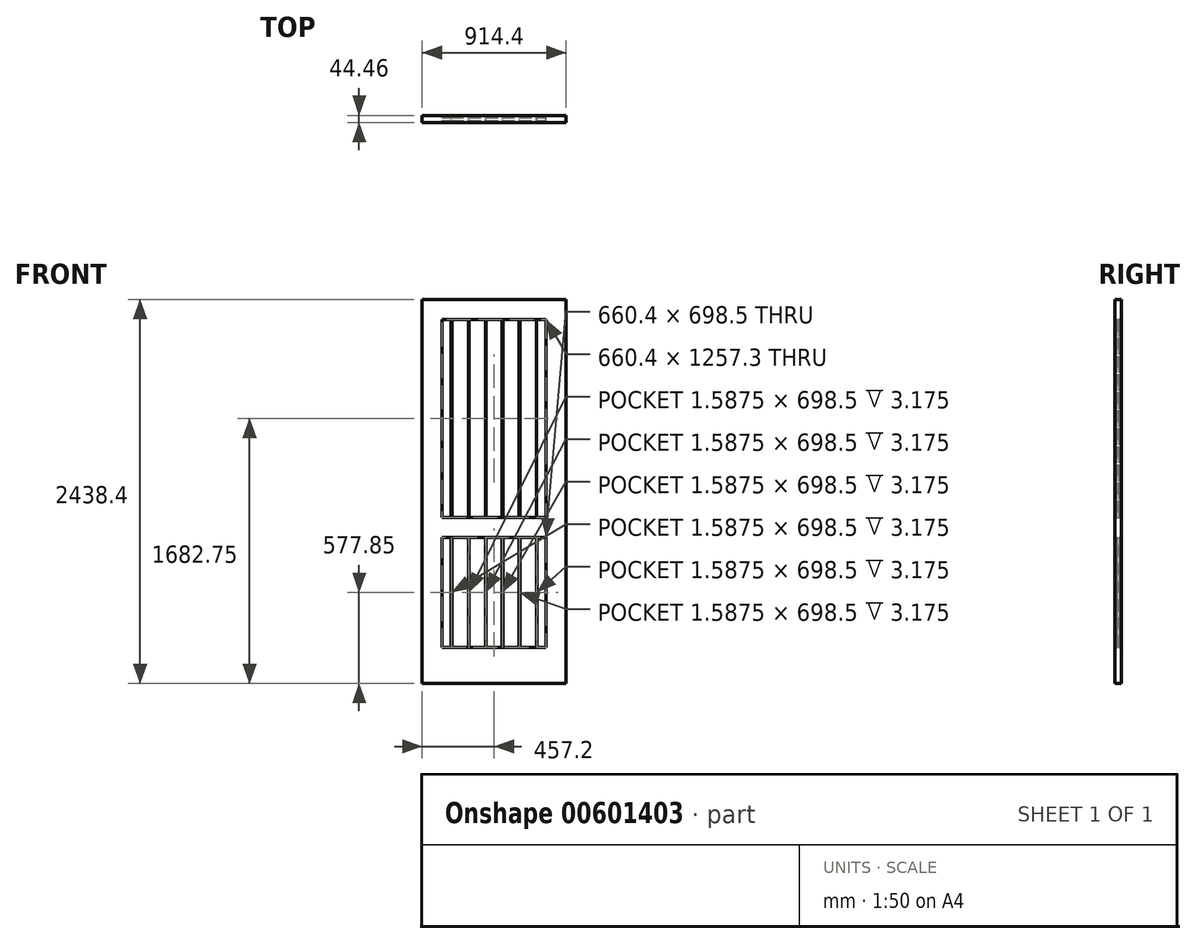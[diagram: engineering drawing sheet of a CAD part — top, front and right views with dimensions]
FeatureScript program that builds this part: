
annotation { "Feature Type Name" : "Feature", "Feature Type Description" : "" }
export const myFeature = defineFeature(function(context is Context, id is Id, definition is map)
    precondition{}
    {
        {
            var Q0;
            Q0=qCreatedBy(makeId("Front.planeOp"),FACE);
            var sketch = newSketch(context, id + "F0", { "sketchPlane" : qUnion([Q0])});
            skLineSegment(sketch, "E0.bottom", {"start": v(-457.2, 1219.2) * mm, "end": v(457.2, 1219.2) * mm});
            skLineSegment(sketch, "E0.top", {"start": v(-457.2, -1219.2) * mm, "end": v(457.2, -1219.2) * mm});
            skLineSegment(sketch, "E0.left", {"start": v(-457.2, 1219.2) * mm, "end": v(-457.2, -1219.2) * mm});
            skLineSegment(sketch, "E0.right", {"start": v(457.2, 1219.2) * mm, "end": v(457.2, -1219.2) * mm});
            skPoint(sketch, "E0.middle", {"position": v(0, 0) * mm});
            skLineSegment(sketch, "E1.bottom", {"start": v(-330.2, 1092.2) * mm, "end": v(330.2, 1092.2) * mm});
            skLineSegment(sketch, "E1.top", {"start": v(-330.2, -990.6) * mm, "end": v(330.2, -990.6) * mm});
            skLineSegment(sketch, "E1.left", {"start": v(-330.2, 1092.2) * mm, "end": v(-330.2, -990.6) * mm});
            skLineSegment(sketch, "E1.right", {"start": v(330.2, 1092.2) * mm, "end": v(330.2, -990.6) * mm});
            skPoint(sketch, "E1.middle", {"position": v(0, 50.8) * mm});
            skLineSegment(sketch, "E2", {"start": v(-330.2, -292.1) * mm, "end": v(330.2, -292.1) * mm});
            skLineSegment(sketch, "E3", {"start": v(-330.2, -165.1) * mm, "end": v(330.2, -165.1) * mm});
            skLineSegment(sketch, "E4", {"start": v(0, 1219.2) * mm, "end": v(0, -990.6) * mm, "construction": true});
            skLineSegment(sketch, "E5", {"start": v(-53.97, 1092.2) * mm, "end": v(-53.98, -165.1) * mm});
            skLineSegment(sketch, "E6", {"start": v(-161.92, 1092.2) * mm, "end": v(-161.92, -165.1) * mm});
            skLineSegment(sketch, "E7", {"start": v(-269.87, 1092.2) * mm, "end": v(-269.87, -165.1) * mm});
            skLineSegment(sketch, "E8.MirrorCS", {"start": v(53.98, 1092.2) * mm, "end": v(53.97, -165.1) * mm});
            skLineSegment(sketch, "E9.MirrorCS", {"start": v(161.92, 1092.2) * mm, "end": v(161.92, -165.1) * mm});
            skLineSegment(sketch, "E10.MirrorCS", {"start": v(269.87, 1092.2) * mm, "end": v(269.87, -165.1) * mm});
            skLineSegment(sketch, "E11", {"start": v(-330.2, -235.67) * mm, "end": v(330.2, -235.67) * mm, "construction": true});
            skLineSegment(sketch, "E12.trimOffspring", {"start": v(-269.88, -990.6) * mm, "end": v(-269.87, -292.1) * mm});
            skLineSegment(sketch, "E13.trimOffspring", {"start": v(-161.93, -990.6) * mm, "end": v(-161.92, -292.1) * mm});
            skLineSegment(sketch, "E14.trimOffspring", {"start": v(-53.97, -990.6) * mm, "end": v(-53.97, -292.1) * mm});
            skLineSegment(sketch, "E15.trimOffspring", {"start": v(53.97, -990.6) * mm, "end": v(53.98, -292.1) * mm});
            skLineSegment(sketch, "E16.trimOffspring", {"start": v(269.87, -990.6) * mm, "end": v(269.88, -292.1) * mm});
            skPoint(sketch, "E17.MirrorCS.start.orphan", {"position": v(-53.98, -1563.55) * mm});
            skPoint(sketch, "E18.MirrorCS.start.orphan", {"position": v(53.97, -1563.55) * mm});
            skPoint(sketch, "E19.MirrorCS.start.orphan", {"position": v(161.93, -1563.55) * mm});
            skPoint(sketch, "E20.MirrorCS.start.orphan", {"position": v(269.88, -1563.55) * mm});
            skPoint(sketch, "E21.MirrorCS.start.orphan", {"position": v(-161.93, -1563.55) * mm});
            skPoint(sketch, "E22.MirrorCS.start.orphan", {"position": v(-269.88, -1563.55) * mm});
            skPoint(sketch, "E23.orphan", {"position": v(0, -1219.2) * mm});
            skLineSegment(sketch, "E24.0", {"start": v(160.34, -1003.3) * mm, "end": v(160.34, -292.1) * mm});
            skLineSegment(sketch, "E25.0.1.0", {"start": v(-271.46, 1092.2) * mm, "end": v(-271.46, -165.1) * mm});
            skLineSegment(sketch, "E25.direction1", {"start": v(-269.88, -165.1) * mm, "end": v(-269.88, -165.1) * mm});
            skLineSegment(sketch, "E25.direction2", {"start": v(-269.88, -165.1) * mm, "end": v(-271.46, -165.1) * mm, "construction": true});
            skLineSegment(sketch, "E26.1.0.0", {"start": v(-160.34, 1092.2) * mm, "end": v(-160.34, -165.1) * mm});
            skLineSegment(sketch, "E26.1.0.1", {"start": v(-52.39, 1092.2) * mm, "end": v(-52.39, -165.1) * mm});
            skLineSegment(sketch, "E26.direction1", {"start": v(-161.92, -165.1) * mm, "end": v(-160.34, -165.1) * mm, "construction": true});
            skLineSegment(sketch, "E27.MirrorCS", {"start": v(52.39, 1092.2) * mm, "end": v(52.39, -165.1) * mm});
            skLineSegment(sketch, "E28.MirrorCS", {"start": v(160.34, 1092.2) * mm, "end": v(160.34, -165.1) * mm});
            skLineSegment(sketch, "E29.MirrorCS", {"start": v(269.88, 1104.9) * mm, "end": v(269.88, -165.1) * mm});
            skLineSegment(sketch, "E30.MirrorCS", {"start": v(271.46, 1092.26) * mm, "end": v(271.46, -177.74) * mm});
            skLineSegment(sketch, "E31.MirrorCS", {"start": v(-269.88, 519.25) * mm, "end": v(-269.88, -165.1) * mm});
            skLineSegment(sketch, "E32.trimOffspring", {"start": v(-271.46, -990.6) * mm, "end": v(-271.46, -292.1) * mm});
            skLineSegment(sketch, "E33.trimOffspring", {"start": v(-160.34, -990.6) * mm, "end": v(-160.34, -292.1) * mm});
            skLineSegment(sketch, "E34.trimOffspring", {"start": v(-52.39, -990.6) * mm, "end": v(-52.39, -292.1) * mm});
            skLineSegment(sketch, "E35.trimOffspring", {"start": v(161.92, -990.6) * mm, "end": v(161.93, -292.1) * mm});
            skLineSegment(sketch, "E36.trimOffspring", {"start": v(52.39, -990.6) * mm, "end": v(52.39, -292.1) * mm});
            skLineSegment(sketch, "E37.trimOffspring", {"start": v(271.46, -990.6) * mm, "end": v(271.46, -292.1) * mm});
            skPoint(sketch, "E38.MirrorCS.start.orphan", {"position": v(52.39, -1563.55) * mm});
            skPoint(sketch, "E39.MirrorCS.start.orphan", {"position": v(161.92, -1563.55) * mm});
            skPoint(sketch, "E40.MirrorCS.start.orphan", {"position": v(160.34, -1563.55) * mm});
            skPoint(sketch, "E41.MirrorCS.start.orphan", {"position": v(271.46, -1563.61) * mm});
            skPoint(sketch, "E42.MirrorCS.start.orphan", {"position": v(269.87, -1563.55) * mm});
            skPoint(sketch, "E43.MirrorCS.start.orphan", {"position": v(-52.39, -1563.55) * mm});
            skPoint(sketch, "E44.MirrorCS.start.orphan", {"position": v(-160.34, -1563.55) * mm});
            skPoint(sketch, "E45.MirrorCS.start.orphan", {"position": v(-271.46, -1563.61) * mm});
            skPoint(sketch, "E46.orphan", {"position": v(-52.39, -306.25) * mm});
            skPoint(sketch, "E47.orphan", {"position": v(-53.97, -306.25) * mm});
            skPoint(sketch, "E48.orphan", {"position": v(53.98, -306.25) * mm});
            skPoint(sketch, "E49.orphan", {"position": v(52.39, -306.25) * mm});
            skPoint(sketch, "E50.orphan", {"position": v(161.92, -306.25) * mm});
            skPoint(sketch, "E51.orphan", {"position": v(271.46, -293.61) * mm});
            skPoint(sketch, "E52.orphan", {"position": v(269.88, -306.25) * mm});
            skPoint(sketch, "E53.orphan", {"position": v(160.34, -306.25) * mm});
            skPoint(sketch, "E54.orphan", {"position": v(-160.34, -306.25) * mm});
            skPoint(sketch, "E55.orphan", {"position": v(-161.92, -306.25) * mm});
            skPoint(sketch, "E56.orphan", {"position": v(-269.87, -306.25) * mm});
            skPoint(sketch, "E57.orphan", {"position": v(-271.46, -293.61) * mm});
            skLineSegment(sketch, "E58.MirrorCS", {"start": v(269.88, 519.25) * mm, "end": v(269.88, -165.1) * mm});
            skLineSegment(sketch, "E59.MirrorCS", {"start": v(271.46, 1092.2) * mm, "end": v(271.46, -165.1) * mm});
            skSolve(sketch);
        }
        {
            var Q0;
            Q0=makeQuery(id+"F0.imprint","IMPRINT",FACE,{"disambiguationData":[TD([[makeQuery(id+"F0.imprint","IMPRINT",EDGE,{"derivedFrom":sQuery(id+"F0.wireOp",EDGE,"E0.bottom")}),-1.0]])]});
            var Q1;
            {var subQ3=sQuery(id+"F0.wireOp",EDGE,"E1.left");var subQ6=sQuery(id+"F0.wireOp",EDGE,"E2");var subQ12=makeQuery(id+"F0.imprint","INTERSECT",VERTEX,{"derivedFrom":[subQ3,subQ6]});Q1=makeQuery(id+"F0.imprint","IMPRINT",FACE,{"disambiguationData":[TD([[makeQuery(id+"F0.imprint","IMPRINT",EDGE,{"disambiguationData":[TD([[subQ12,1.0]])],"derivedFrom":subQ3}),1.0]])]});}
            extrude(context, id + "F1", {"entities" : qUnion([Q0, Q1]), "endBound" : BoundingType.SYMMETRIC, "depth" : 44.45 * mm, "offsetDistance" : 25.4 * mm});
        }
        {
            var Q0;
            {var subQ3=sQuery(id+"F0.wireOp",EDGE,"E32.trimOffspring");Q0=makeQuery(id+"F0.imprint","IMPRINT",FACE,{"disambiguationData":[TD([[makeQuery(id+"F0.imprint","IMPRINT",EDGE,{"derivedFrom":subQ3}),1.0]])]});}
            var Q1;
            {var subQ3=sQuery(id+"F0.wireOp",EDGE,"E37.trimOffspring");Q1=makeQuery(id+"F0.imprint","IMPRINT",FACE,{"disambiguationData":[TD([[makeQuery(id+"F0.imprint","IMPRINT",EDGE,{"derivedFrom":subQ3}),-1.0]])]});}
            var Q2;
            {var subQ0=sQuery(id+"F0.wireOp",EDGE,"E13.trimOffspring");Q2=makeQuery(id+"F0.imprint","IMPRINT",FACE,{"disambiguationData":[TD([[makeQuery(id+"F0.imprint","IMPRINT",EDGE,{"derivedFrom":subQ0}),1.0]])]});}
            var Q3;
            {var subQ0=sQuery(id+"F0.wireOp",EDGE,"E14.trimOffspring");Q3=makeQuery(id+"F0.imprint","IMPRINT",FACE,{"disambiguationData":[TD([[makeQuery(id+"F0.imprint","IMPRINT",EDGE,{"derivedFrom":subQ0}),1.0]])]});}
            var Q4;
            {var subQ0=sQuery(id+"F0.wireOp",EDGE,"E34.trimOffspring");Q4=makeQuery(id+"F0.imprint","IMPRINT",FACE,{"disambiguationData":[TD([[makeQuery(id+"F0.imprint","IMPRINT",EDGE,{"derivedFrom":subQ0}),-1.0]])]});}
            var Q5;
            {var subQ0=sQuery(id+"F0.wireOp",EDGE,"E15.trimOffspring");Q5=makeQuery(id+"F0.imprint","IMPRINT",FACE,{"disambiguationData":[TD([[makeQuery(id+"F0.imprint","IMPRINT",EDGE,{"derivedFrom":subQ0}),-1.0]])]});}
            var Q6;
            {var subQ0=sQuery(id+"F0.wireOp",EDGE,"E35.trimOffspring");Q6=makeQuery(id+"F0.imprint","IMPRINT",FACE,{"disambiguationData":[TD([[makeQuery(id+"F0.imprint","IMPRINT",EDGE,{"derivedFrom":subQ0}),-1.0]])]});}
            var Q7;
            {var subQ4=sQuery(id+"F0.wireOp",EDGE,"E6");Q7=makeQuery(id+"F0.imprint","IMPRINT",FACE,{"disambiguationData":[TD([[makeQuery(id+"F0.imprint","IMPRINT",EDGE,{"derivedFrom":subQ4}),-1.0]])]});}
            var Q8;
            {var subQ0=sQuery(id+"F0.wireOp",EDGE,"E5");Q8=makeQuery(id+"F0.imprint","IMPRINT",FACE,{"disambiguationData":[TD([[makeQuery(id+"F0.imprint","IMPRINT",EDGE,{"derivedFrom":subQ0}),-1.0]])]});}
            var Q9;
            {var subQ0=sQuery(id+"F0.wireOp",EDGE,"E8.MirrorCS");Q9=makeQuery(id+"F0.imprint","IMPRINT",FACE,{"disambiguationData":[TD([[makeQuery(id+"F0.imprint","IMPRINT",EDGE,{"derivedFrom":subQ0}),1.0]])]});}
            var Q10;
            {var subQ0=sQuery(id+"F0.wireOp",EDGE,"E9.MirrorCS");Q10=makeQuery(id+"F0.imprint","IMPRINT",FACE,{"disambiguationData":[TD([[makeQuery(id+"F0.imprint","IMPRINT",EDGE,{"derivedFrom":subQ0}),1.0]])]});}
            var Q11;
            {var subQ0=sQuery(id+"F0.wireOp",EDGE,"E26.1.0.1");Q11=makeQuery(id+"F0.imprint","IMPRINT",FACE,{"disambiguationData":[TD([[makeQuery(id+"F0.imprint","IMPRINT",EDGE,{"derivedFrom":subQ0}),1.0]])]});}
            var Q12;
            {var subQ3=sQuery(id+"F0.wireOp",EDGE,"E25.0.1.0");Q12=makeQuery(id+"F0.imprint","IMPRINT",FACE,{"disambiguationData":[TD([[makeQuery(id+"F0.imprint","IMPRINT",EDGE,{"derivedFrom":subQ3}),-1.0]])]});}
            var Q13;
            {var subQ0=sQuery(id+"F0.wireOp",EDGE,"E59.MirrorCS");var subQ3=makeQuery(id+"F0.imprint","IMPRINT",VERTEX,{"derivedFrom":subQ0});Q13=makeQuery(id+"F0.imprint","IMPRINT",FACE,{"disambiguationData":[TD([[makeQuery(id+"F0.imprint","IMPRINT",EDGE,{"disambiguationData":[TD([[subQ3,1.0]])],"derivedFrom":subQ0}),1.0]])]});}
            var Q14;
            {var subQ3=sQuery(id+"F0.wireOp",EDGE,"E59.MirrorCS");Q14=makeQuery(id+"F0.imprint","IMPRINT",FACE,{"disambiguationData":[TD([[makeQuery(id+"F0.imprint","IMPRINT",EDGE,{"derivedFrom":subQ3}),1.0]])]});}
            extrude(context, id + "F2", {"entities" : qUnion([Q0, Q1, Q2, Q3, Q4, Q5, Q6, Q7, Q8, Q9, Q10, Q11, Q12, Q13, Q14]), "operationType" : NewBodyOperationType.ADD, "endBound" : BoundingType.SYMMETRIC, "depth" : 19.05 * mm, "offsetDistance" : 25.4 * mm});
        }
        {
            var Q0;
            {var subQ1=sQuery(id+"F0.wireOp",EDGE,"E29.MirrorCS");Q0=makeQuery(id+"F0.imprint","IMPRINT",FACE,{"disambiguationData":[TD([[makeQuery(id+"F0.imprint","IMPRINT",EDGE,{"derivedFrom":subQ1}),1.0]])]});}
            var Q1;
            {var subQ0=sQuery(id+"F0.wireOp",EDGE,"E9.MirrorCS");Q1=makeQuery(id+"F0.imprint","IMPRINT",FACE,{"disambiguationData":[TD([[makeQuery(id+"F0.imprint","IMPRINT",EDGE,{"derivedFrom":subQ0}),-1.0]])]});}
            var Q2;
            {var subQ0=sQuery(id+"F0.wireOp",EDGE,"E8.MirrorCS");Q2=makeQuery(id+"F0.imprint","IMPRINT",FACE,{"disambiguationData":[TD([[makeQuery(id+"F0.imprint","IMPRINT",EDGE,{"derivedFrom":subQ0}),-1.0]])]});}
            var Q3;
            {var subQ0=sQuery(id+"F0.wireOp",EDGE,"E5");Q3=makeQuery(id+"F0.imprint","IMPRINT",FACE,{"disambiguationData":[TD([[makeQuery(id+"F0.imprint","IMPRINT",EDGE,{"derivedFrom":subQ0}),1.0]])]});}
            var Q4;
            {var subQ0=sQuery(id+"F0.wireOp",EDGE,"E6");Q4=makeQuery(id+"F0.imprint","IMPRINT",FACE,{"disambiguationData":[TD([[makeQuery(id+"F0.imprint","IMPRINT",EDGE,{"derivedFrom":subQ0}),1.0]])]});}
            var Q5;
            {var subQ6=sQuery(id+"F0.wireOp",EDGE,"E25.0.1.0");Q5=makeQuery(id+"F0.imprint","IMPRINT",FACE,{"disambiguationData":[TD([[makeQuery(id+"F0.imprint","IMPRINT",EDGE,{"derivedFrom":subQ6}),1.0]])]});}
            extrude(context, id + "F3", {"entities" : qUnion([Q0, Q1, Q2, Q3, Q4, Q5]), "operationType" : NewBodyOperationType.ADD, "endBound" : BoundingType.SYMMETRIC, "depth" : 9.52 * mm, "offsetDistance" : 25.4 * mm});
        }
        {
            var Q0;
            {var subQ0=sQuery(id+"F0.wireOp",EDGE,"E12.trimOffspring");Q0=makeQuery(id+"F0.imprint","IMPRINT",FACE,{"disambiguationData":[TD([[makeQuery(id+"F0.imprint","IMPRINT",EDGE,{"derivedFrom":subQ0}),1.0]])]});}
            var Q1;
            {var subQ0=sQuery(id+"F0.wireOp",EDGE,"E13.trimOffspring");Q1=makeQuery(id+"F0.imprint","IMPRINT",FACE,{"disambiguationData":[TD([[makeQuery(id+"F0.imprint","IMPRINT",EDGE,{"derivedFrom":subQ0}),-1.0]])]});}
            var Q2;
            {var subQ0=sQuery(id+"F0.wireOp",EDGE,"E14.trimOffspring");Q2=makeQuery(id+"F0.imprint","IMPRINT",FACE,{"disambiguationData":[TD([[makeQuery(id+"F0.imprint","IMPRINT",EDGE,{"derivedFrom":subQ0}),-1.0]])]});}
            var Q3;
            {var subQ0=sQuery(id+"F0.wireOp",EDGE,"E15.trimOffspring");Q3=makeQuery(id+"F0.imprint","IMPRINT",FACE,{"disambiguationData":[TD([[makeQuery(id+"F0.imprint","IMPRINT",EDGE,{"derivedFrom":subQ0}),1.0]])]});}
            var Q4;
            {var subQ0=sQuery(id+"F0.wireOp",EDGE,"E35.trimOffspring");Q4=makeQuery(id+"F0.imprint","IMPRINT",FACE,{"disambiguationData":[TD([[makeQuery(id+"F0.imprint","IMPRINT",EDGE,{"derivedFrom":subQ0}),1.0]])]});}
            var Q5;
            {var subQ0=sQuery(id+"F0.wireOp",EDGE,"E16.trimOffspring");Q5=makeQuery(id+"F0.imprint","IMPRINT",FACE,{"disambiguationData":[TD([[makeQuery(id+"F0.imprint","IMPRINT",EDGE,{"derivedFrom":subQ0}),-1.0]])]});}
            extrude(context, id + "F4", {"entities" : qUnion([Q0, Q1, Q2, Q3, Q4, Q5]), "operationType" : NewBodyOperationType.ADD, "endBound" : BoundingType.SYMMETRIC, "depth" : 9.52 * mm, "offsetDistance" : 25.4 * mm});
        }
        {
            var Q0;
            Q0=makeQuery(id+"F2.opExtrude","CAP_EDGE",EDGE,{"disambiguationData":[OSD([sQuery(id+"F0.wireOp",EDGE,"E59.MirrorCS")])],"isStart":false});
            var Q1;
            Q1=makeQuery(id+"F2.opExtrude","CAP_EDGE",EDGE,{"disambiguationData":[OSD([sQuery(id+"F0.wireOp",EDGE,"E29.MirrorCS"),sQuery(id+"F0.wireOp",EDGE,"E58.MirrorCS")])],"isStart":false});
            var Q2;
            Q2=makeQuery(id+"F2.opExtrude","CAP_EDGE",EDGE,{"disambiguationData":[OSD([sQuery(id+"F0.wireOp",EDGE,"E9.MirrorCS")])],"isStart":false});
            var Q3;
            Q3=makeQuery(id+"F2.opExtrude","CAP_EDGE",EDGE,{"disambiguationData":[OSD([sQuery(id+"F0.wireOp",EDGE,"E28.MirrorCS")])],"isStart":false});
            var Q4;
            Q4=makeQuery(id+"F2.opExtrude","CAP_EDGE",EDGE,{"disambiguationData":[OSD([sQuery(id+"F0.wireOp",EDGE,"E8.MirrorCS")])],"isStart":false});
            var Q5;
            Q5=makeQuery(id+"F2.opExtrude","CAP_EDGE",EDGE,{"disambiguationData":[OSD([sQuery(id+"F0.wireOp",EDGE,"E27.MirrorCS")])],"isStart":false});
            var Q6;
            Q6=makeQuery(id+"F2.opExtrude","CAP_EDGE",EDGE,{"disambiguationData":[OSD([sQuery(id+"F0.wireOp",EDGE,"E26.1.0.1")])],"isStart":false});
            var Q7;
            Q7=makeQuery(id+"F2.opExtrude","CAP_EDGE",EDGE,{"disambiguationData":[OSD([sQuery(id+"F0.wireOp",EDGE,"E5")])],"isStart":false});
            var Q8;
            Q8=makeQuery(id+"F2.opExtrude","CAP_EDGE",EDGE,{"disambiguationData":[OSD([sQuery(id+"F0.wireOp",EDGE,"E26.1.0.0")])],"isStart":false});
            var Q9;
            Q9=makeQuery(id+"F2.opExtrude","CAP_EDGE",EDGE,{"disambiguationData":[OSD([sQuery(id+"F0.wireOp",EDGE,"E6")])],"isStart":false});
            var Q10;
            Q10=makeQuery(id+"F2.opExtrude","CAP_EDGE",EDGE,{"disambiguationData":[OSD([sQuery(id+"F0.wireOp",EDGE,"E7")])],"isStart":false});
            var Q11;
            Q11=makeQuery(id+"F2.opExtrude","CAP_EDGE",EDGE,{"disambiguationData":[OSD([sQuery(id+"F0.wireOp",EDGE,"E25.0.1.0")])],"isStart":false});
            var Q12;
            Q12=makeQuery(id+"F2.opExtrude","CAP_EDGE",EDGE,{"disambiguationData":[OSD([sQuery(id+"F0.wireOp",EDGE,"E12.trimOffspring")])],"isStart":false});
            var Q13;
            Q13=makeQuery(id+"F2.opExtrude","CAP_EDGE",EDGE,{"disambiguationData":[OSD([sQuery(id+"F0.wireOp",EDGE,"E32.trimOffspring")])],"isStart":false});
            var Q14;
            Q14=makeQuery(id+"F2.opExtrude","CAP_EDGE",EDGE,{"disambiguationData":[OSD([sQuery(id+"F0.wireOp",EDGE,"E13.trimOffspring")])],"isStart":false});
            var Q15;
            Q15=makeQuery(id+"F2.opExtrude","CAP_EDGE",EDGE,{"disambiguationData":[OSD([sQuery(id+"F0.wireOp",EDGE,"E33.trimOffspring")])],"isStart":false});
            var Q16;
            Q16=makeQuery(id+"F2.opExtrude","CAP_EDGE",EDGE,{"disambiguationData":[OSD([sQuery(id+"F0.wireOp",EDGE,"E34.trimOffspring")])],"isStart":false});
            var Q17;
            Q17=makeQuery(id+"F2.opExtrude","CAP_EDGE",EDGE,{"disambiguationData":[OSD([sQuery(id+"F0.wireOp",EDGE,"E14.trimOffspring")])],"isStart":false});
            var Q18;
            Q18=makeQuery(id+"F2.opExtrude","CAP_EDGE",EDGE,{"disambiguationData":[OSD([sQuery(id+"F0.wireOp",EDGE,"E36.trimOffspring")])],"isStart":false});
            var Q19;
            Q19=makeQuery(id+"F2.opExtrude","CAP_EDGE",EDGE,{"disambiguationData":[OSD([sQuery(id+"F0.wireOp",EDGE,"E15.trimOffspring")])],"isStart":false});
            var Q20;
            Q20=makeQuery(id+"F2.opExtrude","CAP_EDGE",EDGE,{"disambiguationData":[OSD([sQuery(id+"F0.wireOp",EDGE,"E24.0")])],"isStart":false});
            var Q21;
            Q21=makeQuery(id+"F2.opExtrude","CAP_EDGE",EDGE,{"disambiguationData":[OSD([sQuery(id+"F0.wireOp",EDGE,"E35.trimOffspring")])],"isStart":false});
            var Q22;
            Q22=makeQuery(id+"F2.opExtrude","CAP_EDGE",EDGE,{"disambiguationData":[OSD([sQuery(id+"F0.wireOp",EDGE,"E16.trimOffspring")])],"isStart":false});
            var Q23;
            Q23=makeQuery(id+"F2.opExtrude","CAP_EDGE",EDGE,{"disambiguationData":[OSD([sQuery(id+"F0.wireOp",EDGE,"E37.trimOffspring")])],"isStart":false});
            var Q24;
            Q24=makeQuery(id+"F2.opExtrude","CAP_EDGE",EDGE,{"disambiguationData":[OSD([sQuery(id+"F0.wireOp",EDGE,"E16.trimOffspring")])],"isStart":true});
            var Q25;
            Q25=makeQuery(id+"F2.opExtrude","CAP_EDGE",EDGE,{"disambiguationData":[OSD([sQuery(id+"F0.wireOp",EDGE,"E37.trimOffspring")])],"isStart":true});
            var Q26;
            Q26=makeQuery(id+"F2.opExtrude","CAP_EDGE",EDGE,{"disambiguationData":[OSD([sQuery(id+"F0.wireOp",EDGE,"E35.trimOffspring")])],"isStart":true});
            var Q27;
            Q27=makeQuery(id+"F2.opExtrude","CAP_EDGE",EDGE,{"disambiguationData":[OSD([sQuery(id+"F0.wireOp",EDGE,"E24.0")])],"isStart":true});
            var Q28;
            Q28=makeQuery(id+"F2.opExtrude","CAP_EDGE",EDGE,{"disambiguationData":[OSD([sQuery(id+"F0.wireOp",EDGE,"E15.trimOffspring")])],"isStart":true});
            var Q29;
            Q29=makeQuery(id+"F2.opExtrude","CAP_EDGE",EDGE,{"disambiguationData":[OSD([sQuery(id+"F0.wireOp",EDGE,"E36.trimOffspring")])],"isStart":true});
            var Q30;
            Q30=makeQuery(id+"F2.opExtrude","CAP_EDGE",EDGE,{"disambiguationData":[OSD([sQuery(id+"F0.wireOp",EDGE,"E34.trimOffspring")])],"isStart":true});
            var Q31;
            Q31=makeQuery(id+"F2.opExtrude","CAP_EDGE",EDGE,{"disambiguationData":[OSD([sQuery(id+"F0.wireOp",EDGE,"E14.trimOffspring")])],"isStart":true});
            var Q32;
            Q32=makeQuery(id+"F2.opExtrude","CAP_EDGE",EDGE,{"disambiguationData":[OSD([sQuery(id+"F0.wireOp",EDGE,"E13.trimOffspring")])],"isStart":true});
            var Q33;
            Q33=makeQuery(id+"F2.opExtrude","CAP_EDGE",EDGE,{"disambiguationData":[OSD([sQuery(id+"F0.wireOp",EDGE,"E33.trimOffspring")])],"isStart":true});
            var Q34;
            Q34=makeQuery(id+"F2.opExtrude","CAP_EDGE",EDGE,{"disambiguationData":[OSD([sQuery(id+"F0.wireOp",EDGE,"E32.trimOffspring")])],"isStart":true});
            var Q35;
            Q35=makeQuery(id+"F2.opExtrude","CAP_EDGE",EDGE,{"disambiguationData":[OSD([sQuery(id+"F0.wireOp",EDGE,"E12.trimOffspring")])],"isStart":true});
            var Q36;
            Q36=makeQuery(id+"F2.opExtrude","CAP_EDGE",EDGE,{"disambiguationData":[OSD([sQuery(id+"F0.wireOp",EDGE,"E59.MirrorCS")])],"isStart":true});
            var Q37;
            Q37=makeQuery(id+"F2.opExtrude","CAP_EDGE",EDGE,{"disambiguationData":[OSD([sQuery(id+"F0.wireOp",EDGE,"E29.MirrorCS"),sQuery(id+"F0.wireOp",EDGE,"E58.MirrorCS")])],"isStart":true});
            var Q38;
            Q38=makeQuery(id+"F2.opExtrude","CAP_EDGE",EDGE,{"disambiguationData":[OSD([sQuery(id+"F0.wireOp",EDGE,"E9.MirrorCS")])],"isStart":true});
            var Q39;
            Q39=makeQuery(id+"F2.opExtrude","CAP_EDGE",EDGE,{"disambiguationData":[OSD([sQuery(id+"F0.wireOp",EDGE,"E28.MirrorCS")])],"isStart":true});
            var Q40;
            Q40=makeQuery(id+"F2.opExtrude","CAP_EDGE",EDGE,{"disambiguationData":[OSD([sQuery(id+"F0.wireOp",EDGE,"E8.MirrorCS")])],"isStart":true});
            var Q41;
            Q41=makeQuery(id+"F2.opExtrude","CAP_EDGE",EDGE,{"disambiguationData":[OSD([sQuery(id+"F0.wireOp",EDGE,"E27.MirrorCS")])],"isStart":true});
            var Q42;
            Q42=makeQuery(id+"F2.opExtrude","CAP_EDGE",EDGE,{"disambiguationData":[OSD([sQuery(id+"F0.wireOp",EDGE,"E26.1.0.1")])],"isStart":true});
            var Q43;
            Q43=makeQuery(id+"F2.opExtrude","CAP_EDGE",EDGE,{"disambiguationData":[OSD([sQuery(id+"F0.wireOp",EDGE,"E5")])],"isStart":true});
            var Q44;
            Q44=makeQuery(id+"F2.opExtrude","CAP_EDGE",EDGE,{"disambiguationData":[OSD([sQuery(id+"F0.wireOp",EDGE,"E26.1.0.0")])],"isStart":true});
            var Q45;
            Q45=makeQuery(id+"F2.opExtrude","CAP_EDGE",EDGE,{"disambiguationData":[OSD([sQuery(id+"F0.wireOp",EDGE,"E6")])],"isStart":true});
            var Q46;
            Q46=makeQuery(id+"F2.opExtrude","CAP_EDGE",EDGE,{"disambiguationData":[OSD([sQuery(id+"F0.wireOp",EDGE,"E25.0.1.0")])],"isStart":true});
            var Q47;
            Q47=makeQuery(id+"F3.opExtrude","CAP_EDGE",EDGE,{"disambiguationData":[OSD([sQuery(id+"F0.wireOp",EDGE,"E7")])],"isStart":true});
            var Q48;
            Q48=makeQuery(id+"F2.opExtrude","CAP_FACE",FACE,{"disambiguationData":[OSD([sQuery(id+"F0.wireOp",EDGE,"E1.bottom"),sQuery(id+"F0.wireOp",EDGE,"E3"),sQuery(id+"F0.wireOp",EDGE,"E6"),sQuery(id+"F0.wireOp",EDGE,"E7")])],"isStart":true});
            chamfer(context, id + "F5", {"entities" : qUnion([Q0, Q1, Q2, Q3, Q4, Q5, Q6, Q7, Q8, Q9, Q10, Q11, Q12, Q13, Q14, Q15, Q16, Q17, Q18, Q19, Q20, Q21, Q22, Q23, Q24, Q25, Q26, Q27, Q28, Q29, Q30, Q31, Q32, Q33, Q34, Q35, Q36, Q37, Q38, Q39, Q40, Q41, Q42, Q43, Q44, Q45, Q46, Q47, Q48]), "width" : 1.59 * mm, "tangentPropagation" : true});
        }
    });
